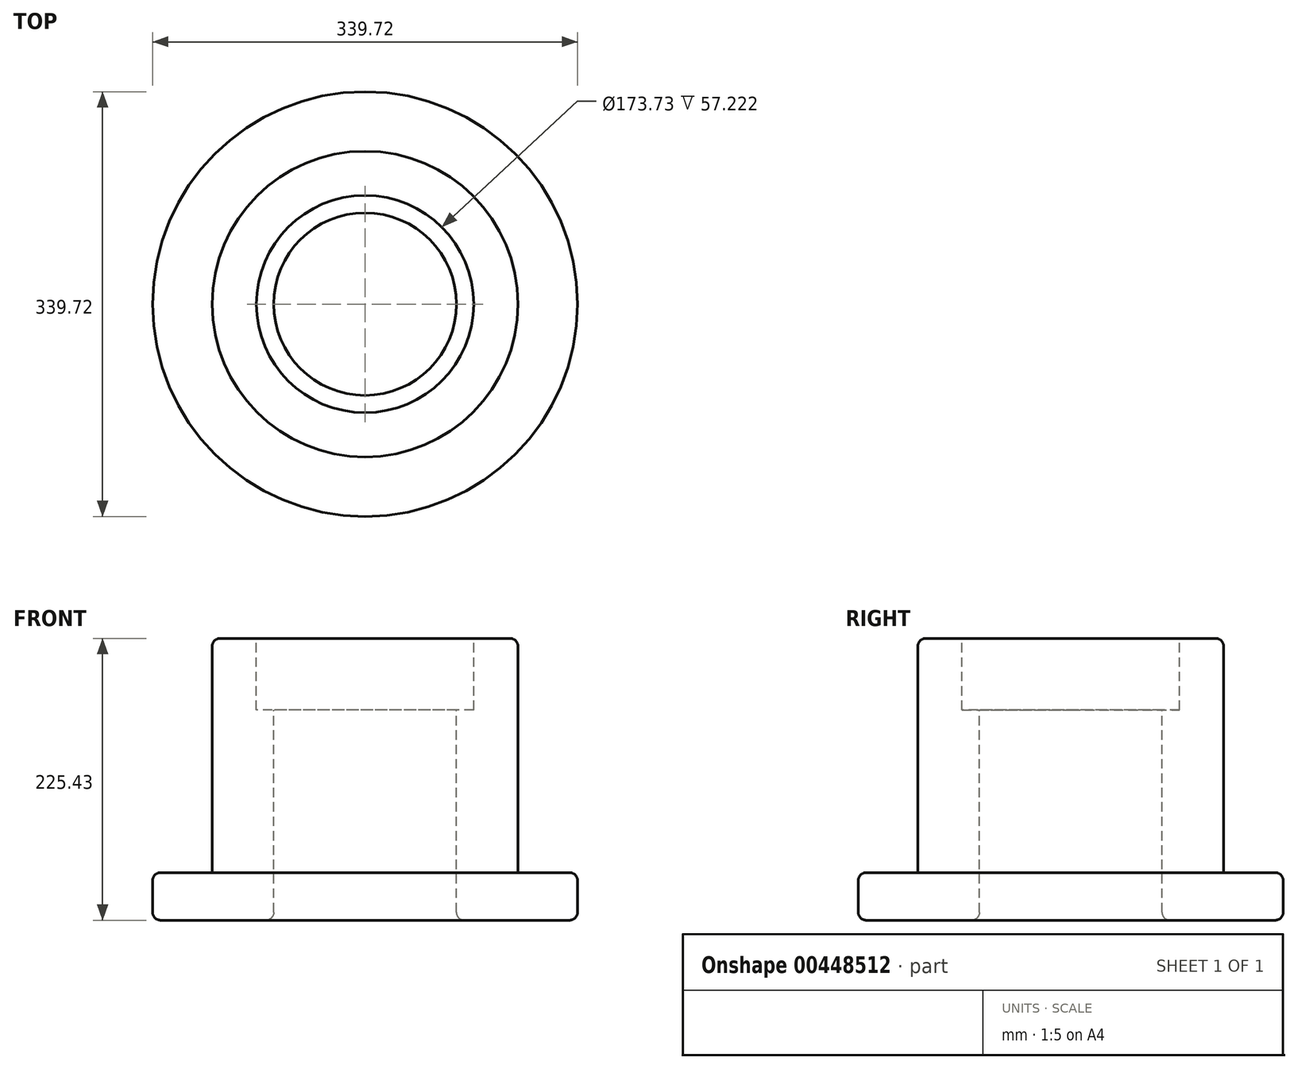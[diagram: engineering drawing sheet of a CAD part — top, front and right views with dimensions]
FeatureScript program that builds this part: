
annotation { "Feature Type Name" : "Feature", "Feature Type Description" : "" }
export const myFeature = defineFeature(function(context is Context, id is Id, definition is map)
    precondition{}
    {
        {
            var Q0;
            Q0=qCreatedBy(makeId("Top.planeOp"),FACE);
            var sketch = newSketch(context, id + "F0", { "sketchPlane" : qUnion([Q0])});
            skCircle(sketch, "E0", {"center": v(0, 0) * mm, "radius": 169.86 * mm});
            skSolve(sketch);
        }
        {
            var Q0;
            Q0 = qSketchRegion(id + "F0", true);
            extrude(context, id + "F1", {"entities" : qUnion([Q0]), "depth" : 38.1 * mm});
        }
        {
            var Q0;
            Q0=makeQuery(id+"F1.opExtrude","CAP_FACE",FACE,{"disambiguationData":[OSD([sQuery(id+"F0.wireOp",EDGE,"E0")])],"isStart":false});
            var sketch = newSketch(context, id + "F2", { "sketchPlane" : qUnion([Q0])});
            skCircle(sketch, "E1", {"center": v(0, 0) * mm, "radius": 122.24 * mm});
            skSolve(sketch);
        }
        {
            var Q0;
            Q0 = qSketchRegion(id + "F2", true);
            extrude(context, id + "F3", {"entities" : qUnion([Q0]), "operationType" : NewBodyOperationType.ADD, "depth" : 187.32 * mm});
        }
        {
            var Q0;
            Q0=makeQuery(id+"F3.opExtrude","CAP_FACE",FACE,{"disambiguationData":[OSD([sQuery(id+"F2.wireOp",EDGE,"E1")])],"isStart":false});
            var sketch = newSketch(context, id + "F4", { "sketchPlane" : qUnion([Q0])});
            skCircle(sketch, "E2", {"center": v(0, 0) * mm, "radius": 73.03 * mm});
            skSolve(sketch);
        }
        {
            var Q0;
            Q0 = qSketchRegion(id + "F4", true);
            extrude(context, id + "F5", {"entities" : qUnion([Q0]), "operationType" : NewBodyOperationType.REMOVE, "endBound" : BoundingType.THROUGH_ALL, "oppositeDirection" : true, "depth" : 25.4 * mm});
        }
        {
            var Q0;
            Q0=makeQuery(id+"F3.opExtrude","CAP_EDGE",EDGE,{"disambiguationData":[OSD([sQuery(id+"F2.wireOp",EDGE,"E1")])],"isStart":false});
            var Q1;
            Q1=makeQuery(id+"F5.boolean.opBoolean","COPY",EDGE,{"derivedFrom":makeQuery(id+"F5.opExtrude","CAP_EDGE",EDGE,{"disambiguationData":[OSD([sQuery(id+"F4.wireOp",EDGE,"E2")])],"isStart":true})});
            var Q2;
            Q2=makeQuery(id+"F3.opExtrude","CAP_EDGE",EDGE,{"disambiguationData":[OSD([sQuery(id+"F2.wireOp",EDGE,"E1")])],"isStart":true});
            var Q3;
            Q3=makeQuery(id+"F1.opExtrude","CAP_EDGE",EDGE,{"disambiguationData":[OSD([sQuery(id+"F0.wireOp",EDGE,"E0")])],"isStart":false});
            var Q4;
            Q4=makeQuery(id+"F1.opExtrude","CAP_EDGE",EDGE,{"disambiguationData":[OSD([sQuery(id+"F0.wireOp",EDGE,"E0")])],"isStart":true});
            var Q5;
            Q5=makeQuery(id+"F5.boolean.opBoolean","INTERSECT",EDGE,{"derivedFrom":[makeQuery(id+"F1.opExtrude","CAP_FACE",FACE,{"disambiguationData":[OSD([sQuery(id+"F0.wireOp",EDGE,"E0")])],"isStart":true}),makeQuery(id+"F5.opExtrude","SWEPT_FACE",FACE,{"disambiguationData":[OSD([sQuery(id+"F4.wireOp",EDGE,"E2")])]})]});
            fillet(context, id + "F6", {"entities" : qUnion([Q0, Q1, Q2, Q3, Q4, Q5]), "radius" : 6.35 * mm, "tangentPropagation" : true, "allowEdgeOverflow" : false});
        }
        {
            var Q0;
            Q0=qCreatedBy(makeId("Front.planeOp"),FACE);
            var sketch = newSketch(context, id + "F7", { "sketchPlane" : qUnion([Q0])});
            skLineSegment(sketch, "E3.0", {"start": v(73.03, 225.43) * mm, "end": v(86.86, 225.43) * mm});
            skLineSegment(sketch, "E4", {"start": v(73.03, 168.2) * mm, "end": v(73.03, 225.43) * mm});
            skLineSegment(sketch, "E5", {"start": v(86.86, 225.43) * mm, "end": v(86.86, 168.2) * mm});
            skLineSegment(sketch, "E6", {"start": v(73.03, 168.2) * mm, "end": v(86.86, 168.2) * mm});
            skLineSegment(sketch, "E7", {"start": v(0, 0) * mm, "end": v(0, 295.56) * mm, "construction": true});
            skSolve(sketch);
        }
        {
            var Q0;
            Q0 = qSketchRegion(id + "F7", true);
            var Q1;
            Q1=sQuery(id+"F7.wireOp",EDGE,"E7");
            revolve(context, id + "F8", {"operationType" : NewBodyOperationType.REMOVE, "entities" : qUnion([Q0]), "axis" : qUnion([Q1]), "revolveType" : RevolveType.FULL, "oppositeDirection" : true});
        }
    });
